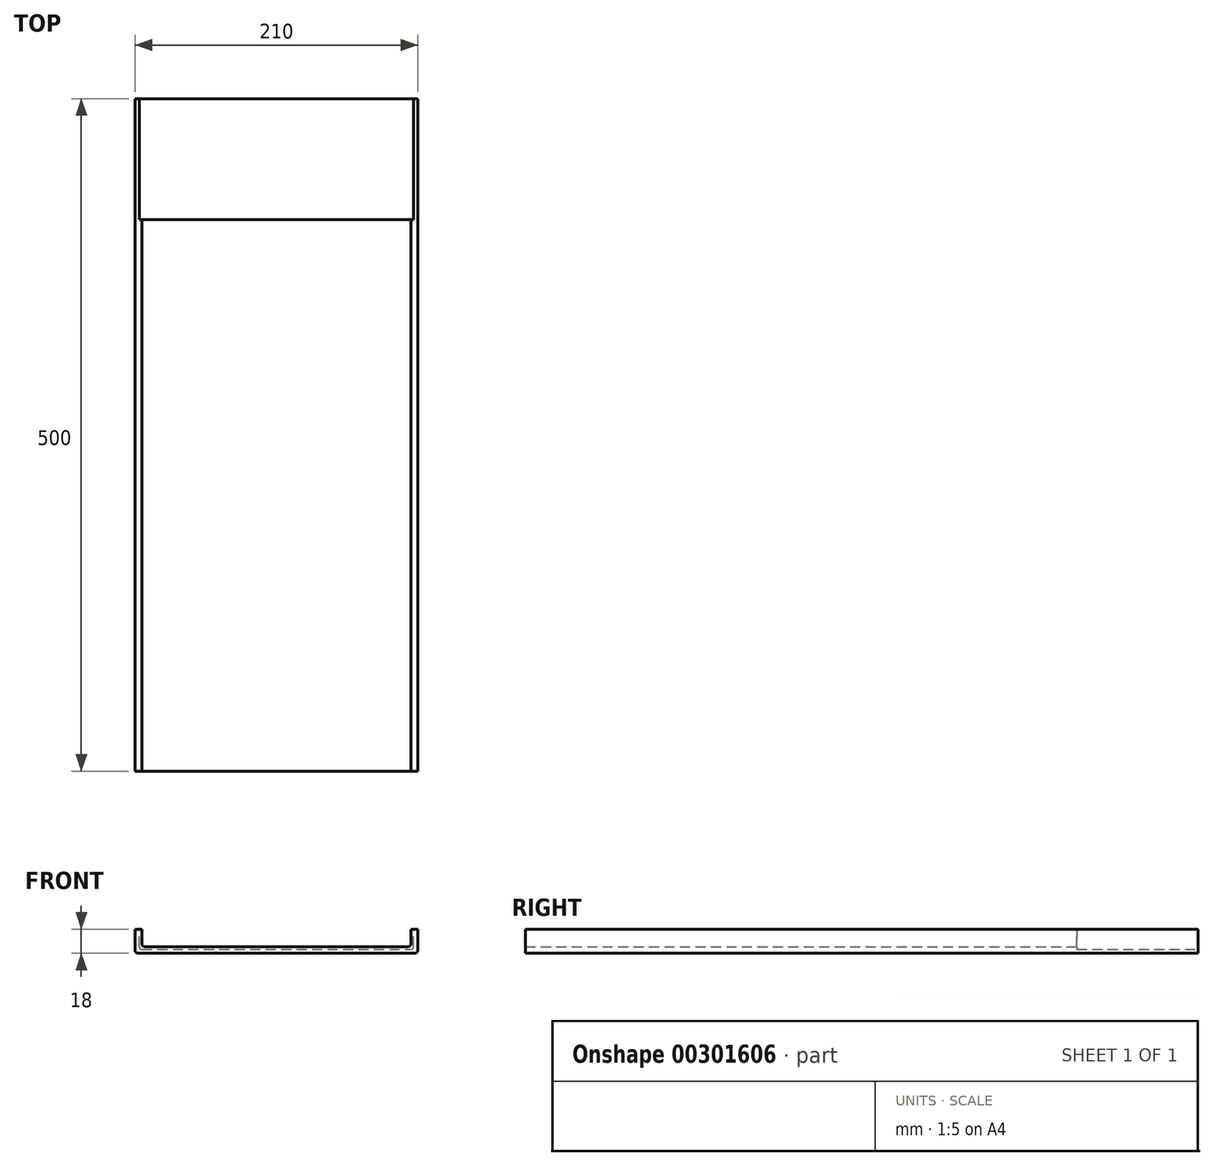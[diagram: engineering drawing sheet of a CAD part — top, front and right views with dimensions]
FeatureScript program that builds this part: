
annotation { "Feature Type Name" : "Feature", "Feature Type Description" : "" }
export const myFeature = defineFeature(function(context is Context, id is Id, definition is map)
    precondition{}
    {
        {
            var Q0;
            Q0=qCreatedBy(makeId("Front.planeOp"),FACE);
            var sketch = newSketch(context, id + "F0", { "sketchPlane" : qUnion([Q0])});
            skLineSegment(sketch, "E0.bottom", {"start": v(100, 0) * mm, "end": v(105, 0) * mm});
            skLineSegment(sketch, "E0.top", {"start": v(0, -18) * mm, "end": v(103, -18) * mm});
            skLineSegment(sketch, "E0.right", {"start": v(105, 0) * mm, "end": v(105, -16) * mm});
            skLineSegment(sketch, "E1.top", {"start": v(0, -13) * mm, "end": v(98, -13) * mm});
            skLineSegment(sketch, "E1.right", {"start": v(100, 0) * mm, "end": v(100, -11) * mm});
            skPoint(sketch, "E2.visualSharp", {"position": v(105, -18) * mm});
            skArc(sketch, "E2.filletArc", {"start": v(103, -18) * mm, "mid": v(104.41, -17.41) * mm, "end": v(105, -16) * mm});
            skPoint(sketch, "E3.visualSharp", {"position": v(100, -13) * mm});
            skArc(sketch, "E3.filletArc", {"start": v(98, -13) * mm, "mid": v(99.41, -12.41) * mm, "end": v(100, -11) * mm});
            skArc(sketch, "E4.MirrorCS", {"start": v(-98, -13) * mm, "mid": v(-99.41, -12.41) * mm, "end": v(-100, -11) * mm});
            skArc(sketch, "E5.MirrorCS", {"start": v(-103, -18) * mm, "mid": v(-104.41, -17.41) * mm, "end": v(-105, -16) * mm});
            skLineSegment(sketch, "E6.MirrorCS", {"start": v(-100, 0) * mm, "end": v(-105, 0) * mm});
            skLineSegment(sketch, "E7.MirrorCS", {"start": v(0, -13) * mm, "end": v(-98, -13) * mm});
            skLineSegment(sketch, "E8.MirrorCS", {"start": v(-100, 0) * mm, "end": v(-100, -11) * mm});
            skLineSegment(sketch, "E9.MirrorCS", {"start": v(-105, 0) * mm, "end": v(-105, -16) * mm});
            skLineSegment(sketch, "E10.MirrorCS", {"start": v(0, -18) * mm, "end": v(-103, -18) * mm});
            skPoint(sketch, "E11.MirrorP", {"position": v(-105, -18) * mm});
            skPoint(sketch, "E12.MirrorP", {"position": v(-100, -13) * mm});
            skLineSegment(sketch, "E13.bottom", {"start": v(-100, -15) * mm, "end": v(100, -15) * mm});
            skLineSegment(sketch, "E13.left", {"start": v(-102, -13) * mm, "end": v(-102, 0) * mm});
            skLineSegment(sketch, "E13.right", {"start": v(102, -13) * mm, "end": v(102, 0) * mm});
            skPoint(sketch, "E13.middle", {"position": v(0, 0) * mm});
            skPoint(sketch, "E14.orphan", {"position": v(-102, 15) * mm});
            skPoint(sketch, "E15.orphan", {"position": v(102, 15) * mm});
            skPoint(sketch, "E16.visualSharp", {"position": v(-102, -15) * mm});
            skArc(sketch, "E16.filletArc", {"start": v(-102, -13) * mm, "mid": v(-101.41, -14.41) * mm, "end": v(-100, -15) * mm});
            skPoint(sketch, "E17.visualSharp", {"position": v(102, -15) * mm});
            skArc(sketch, "E17.filletArc", {"start": v(100, -15) * mm, "mid": v(101.41, -14.41) * mm, "end": v(102, -13) * mm});
            skSolve(sketch);
        }
        {
            var Q0;
            Q0 = qSketchRegion(id + "F0", true);
            extrude(context, id + "F1", {"entities" : qUnion([Q0]), "depth" : 500 * mm});
        }
        {
            var Q0;
            Q0=makeQuery(id+"F0.imprint","IMPRINT",FACE,{"disambiguationData":[TD([[makeQuery(id+"F0.imprint","IMPRINT",EDGE,{"derivedFrom":sQuery(id+"F0.wireOp",EDGE,"E1.top")}),-1.0]])]});
            extrude(context, id + "F2", {"entities" : qUnion([Q0]), "operationType" : NewBodyOperationType.REMOVE, "depth" : 90 * mm});
        }
        {
            var Q0;
            Q0=qCreatedBy(makeId("Front.planeOp"),FACE);
            cPlane(context, id + "F3", {"entities" : qUnion([Q0]), "cplaneType" : CPlaneType.OFFSET, "offset" : 250 * mm, "width" : 150 * mm, "height" : 150 * mm});
        }
    });
